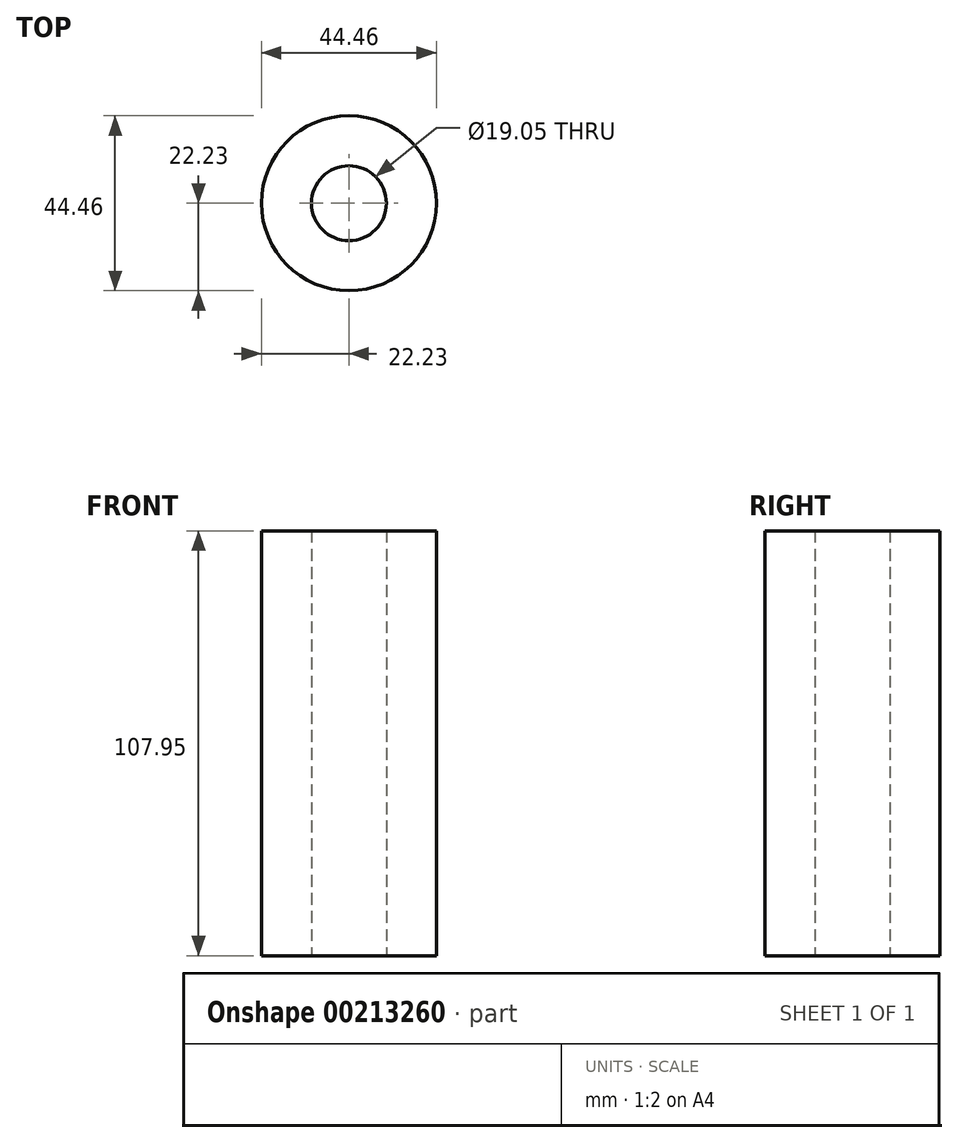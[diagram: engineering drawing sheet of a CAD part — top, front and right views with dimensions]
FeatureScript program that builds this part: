
annotation { "Feature Type Name" : "Feature", "Feature Type Description" : "" }
export const myFeature = defineFeature(function(context is Context, id is Id, definition is map)
    precondition{}
    {
        {
            var Q0;
            Q0=qCreatedBy(makeId("Top.planeOp"),FACE);
            var sketch = newSketch(context, id + "F0", { "sketchPlane" : qUnion([Q0])});
            skCircle(sketch, "E0", {"center": v(0, 0) * mm, "radius": 22.23 * mm});
            skCircle(sketch, "E1", {"center": v(0, 0) * mm, "radius": 9.53 * mm});
            skSolve(sketch);
        }
        {
            var Q0;
            Q0=makeQuery(id+"F0.imprint","IMPRINT",FACE,{"disambiguationData":[TD([[makeQuery(id+"F0.imprint","IMPRINT",EDGE,{"derivedFrom":sQuery(id+"F0.wireOp",EDGE,"E0")}),1.0]])]});
            extrude(context, id + "F1", {"entities" : qUnion([Q0]), "depth" : 107.95 * mm, "offsetDistance" : 25.4 * mm});
        }
        {
            var Q0;
            Q0=qCreatedBy(makeId("Front.planeOp"),FACE);
            cPlane(context, id + "F2", {"entities" : qUnion([Q0]), "cplaneType" : CPlaneType.OFFSET, "offset" : 21.9 * mm, "width" : 152.4 * mm, "height" : 152.4 * mm});
        }
    });
